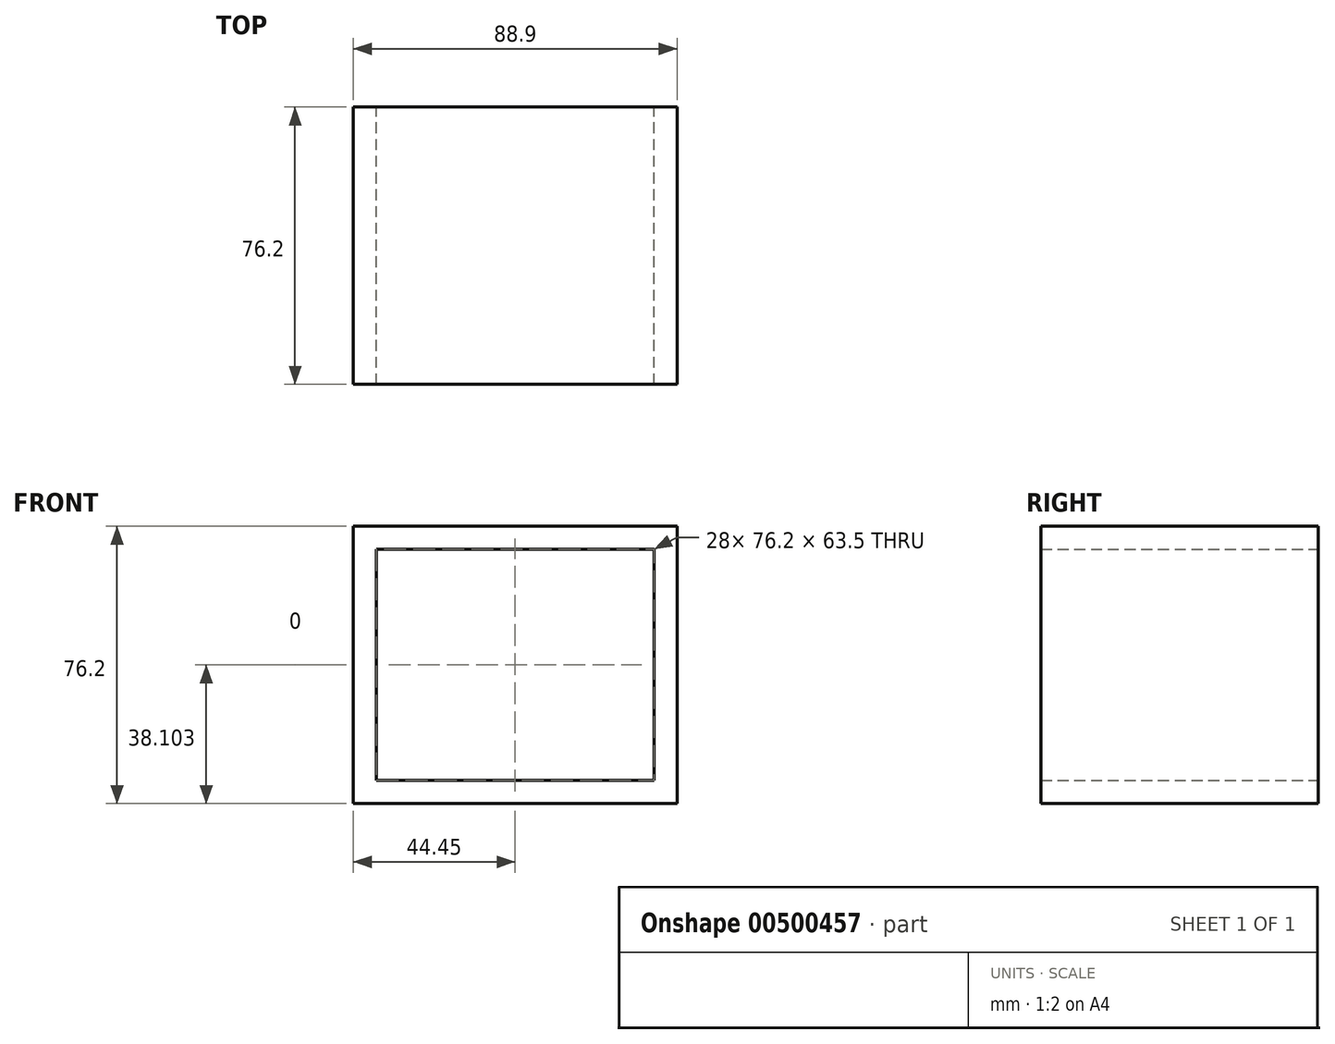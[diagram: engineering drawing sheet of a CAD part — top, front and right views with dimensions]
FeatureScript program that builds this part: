
annotation { "Feature Type Name" : "Feature", "Feature Type Description" : "" }
export const myFeature = defineFeature(function(context is Context, id is Id, definition is map)
    precondition{}
    {
        {
            var Q0;
            Q0=qCreatedBy(makeId("Front.planeOp"),FACE);
            var sketch = newSketch(context, id + "F0", { "sketchPlane" : qUnion([Q0])});
            skLineSegment(sketch, "E0.bottom", {"start": v(-95.39, 40.35) * mm, "end": v(-6.49, 40.35) * mm});
            skLineSegment(sketch, "E0.top", {"start": v(-95.39, -35.85) * mm, "end": v(-6.49, -35.85) * mm});
            skLineSegment(sketch, "E0.left", {"start": v(-95.39, 40.35) * mm, "end": v(-95.39, -35.85) * mm});
            skLineSegment(sketch, "E0.right", {"start": v(-6.49, 40.35) * mm, "end": v(-6.49, -35.85) * mm});
            skLineSegment(sketch, "E1.bottom", {"start": v(-89.04, 34) * mm, "end": v(-12.84, 34) * mm});
            skLineSegment(sketch, "E1.top", {"start": v(-89.04, -29.5) * mm, "end": v(-12.84, -29.5) * mm});
            skLineSegment(sketch, "E1.left", {"start": v(-89.04, 34) * mm, "end": v(-89.04, -29.5) * mm});
            skLineSegment(sketch, "E1.right", {"start": v(-12.84, 34) * mm, "end": v(-12.84, -29.5) * mm});
            skSolve(sketch);
        }
        {
            var Q0;
            Q0=makeQuery(id+"F0.imprint","IMPRINT",FACE,{"disambiguationData":[TD([[makeQuery(id+"F0.imprint","IMPRINT",EDGE,{"derivedFrom":sQuery(id+"F0.wireOp",EDGE,"E0.bottom")}),-1.0]])]});
            extrude(context, id + "F1", {"entities" : qUnion([Q0]), "depth" : 76.2 * mm});
        }
    });
